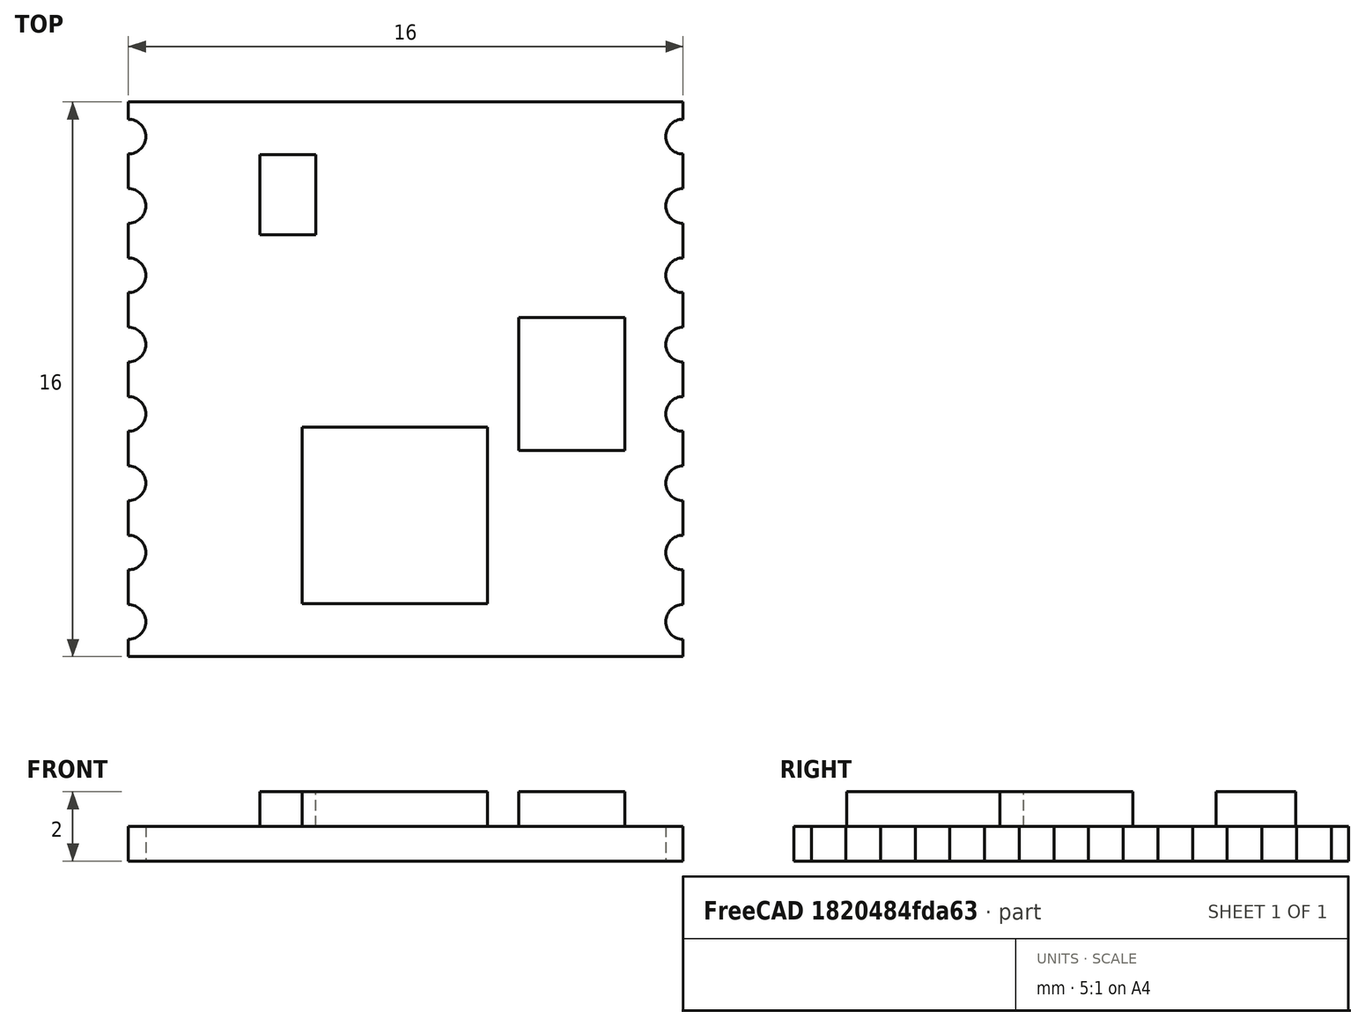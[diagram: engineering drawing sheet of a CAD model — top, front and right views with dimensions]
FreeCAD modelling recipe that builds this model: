
FCSTD DOCUMENT  (FreeCAD 0.19R24267 +99 (Git))
Label: rf_pcb
License: All rights reserved
LicenseURL: http://en.wikipedia.org/wiki/All_rights_reserved
objects: Part::Part2DObjectPython×20, Part::Mirroring×16, Sketcher::SketchObject×3, Part::Extrusion×3, Part::Fuse×2, PartDesign::FeatureBase×1, PartDesign::Body×1
note: 46 computed .brp shape members not serialized (recipe doc carries the construction recipe); baked Part::Feature solids carry a one-line shape summary decoded from their .brp

FEATURE [Part::Part2DObjectPython] Line  # Draft 2D object (typed FeaturePython)
  Area = 0
  ChamferSize = 0
  Closed = false
  End = (8,8,0)
  FilletRadius = 0
  Length = 16
  MakeFace = false
  Placement = pos=(-8,8,0) rot=(0,0,1;0rad)
  Points = (2) [(0,0,0),(16,8.88178e-16,0)]
  Start = (-8,8,0)
  Subdivisions = 0
FEATURE [Part::Part2DObjectPython] Line001  # Draft 2D object (typed FeaturePython)
  Area = 0
  ChamferSize = 0
  Closed = false
  End = (8,-8,0)
  FilletRadius = 0
  Length = 16
  MakeFace = false
  Placement = pos=(-8,-8,0) rot=(0,0,1;0rad)
  Points = (2) [(0,0,0),(16,3.55271e-15,0)]
  Start = (-8,-8,0)
  Subdivisions = 0
FEATURE [Part::Part2DObjectPython] Arc  # Draft 2D object (typed FeaturePython)
  Area = 0
  FirstAngle = -90
  LastAngle = 90
  MakeFace = false
  Placement = pos=(-8,-7,0) rot=(0,0,1;0rad)
  Radius = 0.5
FEATURE [Part::Part2DObjectPython] Arc001 .. Arc007  x7 (patterned run collapsed; names and placements below)
  Area = 0
  FirstAngle = -90
  LastAngle = 90
  MakeFace = false
  Radius = 0.5
  placements: 7 in arithmetic series — first pos=(-8,-5,0) rot=(0,0,1;0rad), step (0,2,0), last pos=(-8,7,0) rot=(0,0,1;0rad)
FEATURE [Part::Part2DObjectPython] Line003  # Draft 2D object (typed FeaturePython)
  Area = 0
  ChamferSize = 0
  Closed = false
  End = (-8,6.5,0)
  FilletRadius = 0
  Length = 1
  MakeFace = false
  Placement = pos=(-8,5.5,0) rot=(0,0,1;0rad)
  Points = (2) [(0,0,0),(0,1,0)]
  Start = (-8,5.5,0)
  Subdivisions = 0
FEATURE [Part::Part2DObjectPython] Line004  # Draft 2D object (typed FeaturePython)
  Area = 0
  ChamferSize = 0
  Closed = false
  End = (-8,4.5,0)
  FilletRadius = 0
  Length = 1
  MakeFace = false
  Placement = pos=(-8,3.5,0) rot=(0,0,1;0rad)
  Points = (2) [(0,0,0),(0,1,0)]
  Start = (-8,3.5,0)
  Subdivisions = 0
FEATURE [Part::Part2DObjectPython] Line005  # Draft 2D object (typed FeaturePython)
  Area = 0
  ChamferSize = 0
  Closed = false
  End = (-8,2.5,0)
  FilletRadius = 0
  Length = 1
  MakeFace = false
  Placement = pos=(-8,1.5,0) rot=(0,0,1;0rad)
  Points = (2) [(0,0,0),(0,1,0)]
  Start = (-8,1.5,0)
  Subdivisions = 0
FEATURE [Part::Part2DObjectPython] Line006  # Draft 2D object (typed FeaturePython)
  Area = 0
  ChamferSize = 0
  Closed = false
  End = (-8,0.5,0)
  FilletRadius = 0
  Length = 1
  MakeFace = false
  Placement = pos=(-8,-0.5,0) rot=(0,0,1;0rad)
  Points = (2) [(0,0,0),(0,1,0)]
  Start = (-8,-0.5,0)
  Subdivisions = 0
FEATURE [Part::Part2DObjectPython] Line007  # Draft 2D object (typed FeaturePython)
  Area = 0
  ChamferSize = 0
  Closed = false
  End = (-8,-1.5,0)
  FilletRadius = 0
  Length = 1
  MakeFace = false
  Placement = pos=(-8,-2.5,0) rot=(0,0,1;0rad)
  Points = (2) [(0,0,0),(0,1,0)]
  Start = (-8,-2.5,0)
  Subdivisions = 0
FEATURE [Part::Part2DObjectPython] Line008  # Draft 2D object (typed FeaturePython)
  Area = 0
  ChamferSize = 0
  Closed = false
  End = (-8,-3.5,0)
  FilletRadius = 0
  Length = 1
  MakeFace = false
  Placement = pos=(-8,-4.5,0) rot=(0,0,1;0rad)
  Points = (2) [(0,0,0),(0,1,0)]
  Start = (-8,-4.5,0)
  Subdivisions = 0
FEATURE [Part::Part2DObjectPython] Line009  # Draft 2D object (typed FeaturePython)
  Area = 0
  ChamferSize = 0
  Closed = false
  End = (-8,-5.5,0)
  FilletRadius = 0
  Length = 1
  MakeFace = false
  Placement = pos=(-8,-6.5,0) rot=(0,0,1;0rad)
  Points = (2) [(0,0,0),(0,1,0)]
  Start = (-8,-6.5,0)
  Subdivisions = 0
FEATURE [Part::Part2DObjectPython] Line010  # Draft 2D object (typed FeaturePython)
  Area = 0
  ChamferSize = 0
  Closed = false
  End = (-8,-7.5,0)
  FilletRadius = 0
  Length = 0.5
  MakeFace = false
  Placement = pos=(-8,-8,0) rot=(0,0,1;0rad)
  Points = (2) [(0,0,0),(0,0.5,0)]
  Start = (-8,-8,0)
  Subdivisions = 0
FEATURE [Part::Mirroring] mirror  label="Arc (mirrored)"
  Base = (0,-7,0)
  Normal = (1,0,0)
  Source = -> Arc
FEATURE [Part::Mirroring] mirror001  label="Arc001 (mirrored)"
  Base = (0,-7,0)
  Normal = (1,0,0)
  Source = -> Arc001
FEATURE [Part::Mirroring] mirror002  label="Arc002 (mirrored)"
  Base = (0,-7,0)
  Normal = (1,0,0)
  Source = -> Arc002
FEATURE [Part::Mirroring] mirror003  label="Arc003 (mirrored)"
  Base = (0,-7,0)
  Normal = (1,0,0)
  Source = -> Arc003
FEATURE [Part::Mirroring] mirror004  label="Arc004 (mirrored)"
  Base = (0,-7,0)
  Normal = (1,0,0)
  Source = -> Arc004
FEATURE [Part::Mirroring] mirror005  label="Arc005 (mirrored)"
  Base = (0,-7,0)
  Normal = (1,0,0)
  Source = -> Arc005
FEATURE [Part::Mirroring] mirror006  label="Arc006 (mirrored)"
  Base = (0,-7,0)
  Normal = (1,0,0)
  Source = -> Arc006
FEATURE [Part::Mirroring] mirror007  label="Arc007 (mirrored)"
  Base = (0,-7,0)
  Normal = (1,0,0)
  Source = -> Arc007
FEATURE [Part::Mirroring] mirror009  label="Line003 (mirrored)"
  Base = (0,-7,0)
  Normal = (1,0,0)
  Source = -> Line003
FEATURE [Part::Mirroring] mirror010  label="Line004 (mirrored)"
  Base = (0,-7,0)
  Normal = (1,0,0)
  Source = -> Line004
FEATURE [Part::Mirroring] mirror011  label="Line005 (mirrored)"
  Base = (0,-7,0)
  Normal = (1,0,0)
  Source = -> Line005
FEATURE [Part::Mirroring] mirror012  label="Line006 (mirrored)"
  Base = (0,-7,0)
  Normal = (1,0,0)
  Source = -> Line006
FEATURE [Part::Mirroring] mirror013  label="Line007 (mirrored)"
  Base = (0,-7,0)
  Normal = (1,0,0)
  Source = -> Line007
FEATURE [Part::Mirroring] mirror014  label="Line008 (mirrored)"
  Base = (0,-7,0)
  Normal = (1,0,0)
  Source = -> Line008
FEATURE [Part::Mirroring] mirror015  label="Line009 (mirrored)"
  Base = (0,-7,0)
  Normal = (1,0,0)
  Source = -> Line009
FEATURE [Part::Mirroring] mirror016  label="Line010 (mirrored)"
  Base = (0,-7,0)
  Normal = (1,0,0)
  Source = -> Line010
FEATURE [Part::Part2DObjectPython] Line011  # Draft 2D object (typed FeaturePython)
  Area = 0
  ChamferSize = 0
  Closed = false
  End = (-8,8,0)
  FilletRadius = 0
  Length = 0.5
  MakeFace = false
  Placement = pos=(-8,7.5,0) rot=(0,0,1;0rad)
  Points = (2) [(0,0,0),(0,0.5,0)]
  Start = (-8,7.5,0)
  Subdivisions = 0
FEATURE [Part::Part2DObjectPython] Line012  # Draft 2D object (typed FeaturePython)
  Area = 0
  ChamferSize = 0
  Closed = false
  End = (8,8,0)
  FilletRadius = 0
  Length = 0.5
  MakeFace = false
  Placement = pos=(8,7.5,0) rot=(0,0,1;0rad)
  Points = (2) [(0,0,0),(0,0.5,0)]
  Start = (8,7.5,0)
  Subdivisions = 0
FEATURE [Sketcher::SketchObject] Sketch
  FullyConstrained = false
  sketch-geometry (36):
    g0: ArcOfCircle CenterX=-8 CenterY=5 CenterZ=0 NormalX=0 NormalY=0 NormalZ=1 AngleXU=0 Radius=0.5 StartAngle=4.71239 EndAngle=7.85398
    g1: ArcOfCircle CenterX=-8 CenterY=7 CenterZ=0 NormalX=0 NormalY=0 NormalZ=1 AngleXU=0 Radius=0.5 StartAngle=4.71239 EndAngle=7.85398
    g2: LineSegment StartX=-8 StartY=3.5 StartZ=0 EndX=-8 EndY=4.5 EndZ=0
    g3: LineSegment StartX=-8 StartY=-0.5 StartZ=0 EndX=-8 EndY=0.5 EndZ=0
    g4: LineSegment StartX=-8 StartY=-8 StartZ=0 EndX=8 EndY=-8 EndZ=0
    g5: ArcOfCircle CenterX=-8 CenterY=1 CenterZ=0 NormalX=0 NormalY=0 NormalZ=1 AngleXU=0 Radius=0.5 StartAngle=4.71239 EndAngle=7.85398
    g6: ArcOfCircle CenterX=-8 CenterY=-7 CenterZ=0 NormalX=0 NormalY=0 NormalZ=1 AngleXU=0 Radius=0.5 StartAngle=4.71239 EndAngle=7.85398
    g7: ArcOfCircle CenterX=-8 CenterY=-3 CenterZ=0 NormalX=0 NormalY=0 NormalZ=1 AngleXU=0 Radius=0.5 StartAngle=4.71239 EndAngle=7.85398
    g8: ArcOfCircle CenterX=-8 CenterY=-5 CenterZ=0 NormalX=0 NormalY=0 NormalZ=1 AngleXU=0 Radius=0.5 StartAngle=4.71239 EndAngle=7.85398
    g9: ArcOfCircle CenterX=-8 CenterY=-1 CenterZ=0 NormalX=0 NormalY=0 NormalZ=1 AngleXU=0 Radius=0.5 StartAngle=4.71239 EndAngle=7.85398
    g10: ArcOfCircle CenterX=-8 CenterY=3 CenterZ=0 NormalX=0 NormalY=0 NormalZ=1 AngleXU=0 Radius=0.5 StartAngle=4.71239 EndAngle=7.85398
    g11: LineSegment StartX=-8 StartY=5.5 StartZ=0 EndX=-8 EndY=6.5 EndZ=0
    g12: LineSegment StartX=-8 StartY=1.5 StartZ=0 EndX=-8 EndY=2.5 EndZ=0
    g13: LineSegment StartX=-8 StartY=-2.5 StartZ=0 EndX=-8 EndY=-1.5 EndZ=0
    g14: LineSegment StartX=-8 StartY=-4.5 StartZ=0 EndX=-8 EndY=-3.5 EndZ=0
    g15: LineSegment StartX=-8 StartY=-6.5 StartZ=0 EndX=-8 EndY=-5.5 EndZ=0
    g16: LineSegment StartX=-8 StartY=-8 StartZ=0 EndX=-8 EndY=-7.5 EndZ=0
    g17: LineSegment StartX=8 StartY=-0.5 StartZ=0 EndX=8 EndY=0.5 EndZ=0
    g18: LineSegment StartX=8 StartY=5.5 StartZ=0 EndX=8 EndY=6.5 EndZ=0
    g19: LineSegment StartX=8 StartY=1.5 StartZ=0 EndX=8 EndY=2.5 EndZ=0
    g20: LineSegment StartX=8 StartY=3.5 StartZ=0 EndX=8 EndY=4.5 EndZ=0
    g21: LineSegment StartX=8 StartY=-6.5 StartZ=0 EndX=8 EndY=-5.5 EndZ=0
    g22: LineSegment StartX=8 StartY=-2.5 StartZ=0 EndX=8 EndY=-1.5 EndZ=0
    g23: LineSegment StartX=8 StartY=-4.5 StartZ=0 EndX=8 EndY=-3.5 EndZ=0
    g24: LineSegment StartX=8 StartY=-8 StartZ=0 EndX=8 EndY=-7.5 EndZ=0
    g25: LineSegment StartX=8 StartY=7.5 StartZ=0 EndX=8 EndY=8 EndZ=0
    g26: LineSegment StartX=-8 StartY=7.5 StartZ=0 EndX=-8 EndY=8 EndZ=0
    g27: ArcOfCircle CenterX=8 CenterY=-3 CenterZ=0 NormalX=0 NormalY=0 NormalZ=1 AngleXU=-3.14159 Radius=0.5 StartAngle=4.71239 EndAngle=7.85398
    g28: ArcOfCircle CenterX=8 CenterY=-1 CenterZ=0 NormalX=0 NormalY=0 NormalZ=1 AngleXU=-3.14159 Radius=0.5 StartAngle=4.71239 EndAngle=7.85398
    g29: ArcOfCircle CenterX=8 CenterY=1 CenterZ=0 NormalX=0 NormalY=0 NormalZ=1 AngleXU=-3.14159 Radius=0.5 StartAngle=4.71239 EndAngle=7.85398
    g30: ArcOfCircle CenterX=8 CenterY=-7 CenterZ=0 NormalX=0 NormalY=0 NormalZ=1 AngleXU=3.14159 Radius=0.5 StartAngle=4.71239 EndAngle=7.85398
    g31: ArcOfCircle CenterX=8 CenterY=3 CenterZ=0 NormalX=0 NormalY=0 NormalZ=1 AngleXU=-3.14159 Radius=0.5 StartAngle=4.71239 EndAngle=7.85398
    g32: ArcOfCircle CenterX=8 CenterY=5 CenterZ=0 NormalX=0 NormalY=0 NormalZ=1 AngleXU=-3.14159 Radius=0.5 StartAngle=4.71239 EndAngle=7.85398
    g33: ArcOfCircle CenterX=8 CenterY=7 CenterZ=0 NormalX=0 NormalY=0 NormalZ=1 AngleXU=-3.14159 Radius=0.5 StartAngle=4.71239 EndAngle=7.85398
    g34: ArcOfCircle CenterX=8 CenterY=-5 CenterZ=0 NormalX=0 NormalY=0 NormalZ=1 AngleXU=-3.14159 Radius=0.5 StartAngle=4.71239 EndAngle=7.85398
    g35: LineSegment StartX=-8 StartY=8 StartZ=0 EndX=8 EndY=8 EndZ=0
  constraints (8):
    c: Vertical(g17)
    c: Vertical(g18)
    c: Vertical(g19)
    c: Vertical(g20)
    c: Vertical(g21)
    c: Vertical(g22)
    c: Vertical(g23)
    c: Vertical(g24)
FEATURE [Part::Extrusion] Extrude
  Base = -> Sketch
  Dir = (0,0,1)
  DirMode = 2
  FaceMakerClass = Part::FaceMakerBullseye
  LengthFwd = 1
  LengthRev = 0
  Solid = true
  Symmetric = false
FEATURE [PartDesign::FeatureBase] BaseFeature
  BaseFeature = -> Extrude
FEATURE [Sketcher::SketchObject] Sketch001
  FullyConstrained = false
  MapMode = 5
  Placement = pos=(0,0,1) rot=(0,0,1;0rad)
  Support = -> [BaseFeature]
  sketch-geometry (4):
    g0: LineSegment StartX=-2.98891 StartY=-1.37693 StartZ=0 EndX=2.35726 EndY=-1.37693 EndZ=0
    g1: LineSegment StartX=2.35726 StartY=-1.37693 StartZ=0 EndX=2.35726 EndY=-6.47787 EndZ=0
    g2: LineSegment StartX=2.35726 StartY=-6.47787 StartZ=0 EndX=-2.98891 EndY=-6.47787 EndZ=0
    g3: LineSegment StartX=-2.98891 StartY=-6.47787 StartZ=0 EndX=-2.98891 EndY=-1.37693 EndZ=0
  constraints (8):
    c: Coincident(g0,g1)
    c: Coincident(g1,g2)
    c: Coincident(g2,g3)
    c: Coincident(g3,g0)
    c: Horizontal(g0)
    c: Horizontal(g2)
    c: Vertical(g1)
    c: Vertical(g3)
FEATURE [Sketcher::SketchObject] Sketch002
  FullyConstrained = false
  MapMode = 5
  Placement = pos=(0,0,1) rot=(0,0,1;0rad)
  Support = -> [BaseFeature]
  sketch-geometry (8):
    g0: LineSegment StartX=3.2629 StartY=1.78264 StartZ=0 EndX=6.3148 EndY=1.78264 EndZ=0
    g1: LineSegment StartX=6.3148 StartY=1.78264 StartZ=0 EndX=6.3148 EndY=-2.05232 EndZ=0
    g2: LineSegment StartX=6.3148 StartY=-2.05232 StartZ=0 EndX=3.2629 EndY=-2.05232 EndZ=0
    g3: LineSegment StartX=3.2629 StartY=-2.05232 StartZ=0 EndX=3.2629 EndY=1.78264 EndZ=0
    g4: LineSegment StartX=-4.20624 StartY=6.48097 StartZ=0 EndX=-2.59997 EndY=6.48097 EndZ=0
    g5: LineSegment StartX=-2.59997 StartY=6.48097 StartZ=0 EndX=-2.59997 EndY=4.17196 EndZ=0
    g6: LineSegment StartX=-2.59997 StartY=4.17196 StartZ=0 EndX=-4.20624 EndY=4.17196 EndZ=0
    g7: LineSegment StartX=-4.20624 StartY=4.17196 StartZ=0 EndX=-4.20624 EndY=6.48097 EndZ=0
  constraints (16):
    c: Coincident(g0,g1)
    c: Coincident(g1,g2)
    c: Coincident(g2,g3)
    c: Coincident(g3,g0)
    c: Horizontal(g0)
    c: Horizontal(g2)
    c: Vertical(g1)
    c: Vertical(g3)
    c: Coincident(g4,g5)
    c: Coincident(g5,g6)
    c: Coincident(g6,g7)
    c: Coincident(g7,g4)
    c: Horizontal(g4)
    c: Horizontal(g6)
    c: Vertical(g5)
    c: Vertical(g7)
FEATURE [PartDesign::Body] Body
  BaseFeature = -> Extrude
  Group = -> [BaseFeature,Sketch001,Sketch002]
  Origin = -> Origin
  Tip = -> BaseFeature
FEATURE [Part::Extrusion] Extrude001
  Base = -> Sketch002
  Dir = (0,0,1)
  DirMode = 2
  FaceMakerClass = Part::FaceMakerBullseye
  LengthFwd = 1
  LengthRev = 0
  Solid = true
  Symmetric = false
FEATURE [Part::Extrusion] Extrude002
  Base = -> Sketch001
  Dir = (0,0,1)
  DirMode = 2
  FaceMakerClass = Part::FaceMakerBullseye
  LengthFwd = 1
  LengthRev = 0
  Solid = true
  Symmetric = false
FEATURE [Part::Fuse] Fusion
  Base = -> Body
  Tool = -> Extrude001
FEATURE [Part::Fuse] Fusion001
  Base = -> Extrude002
  Tool = -> Fusion
